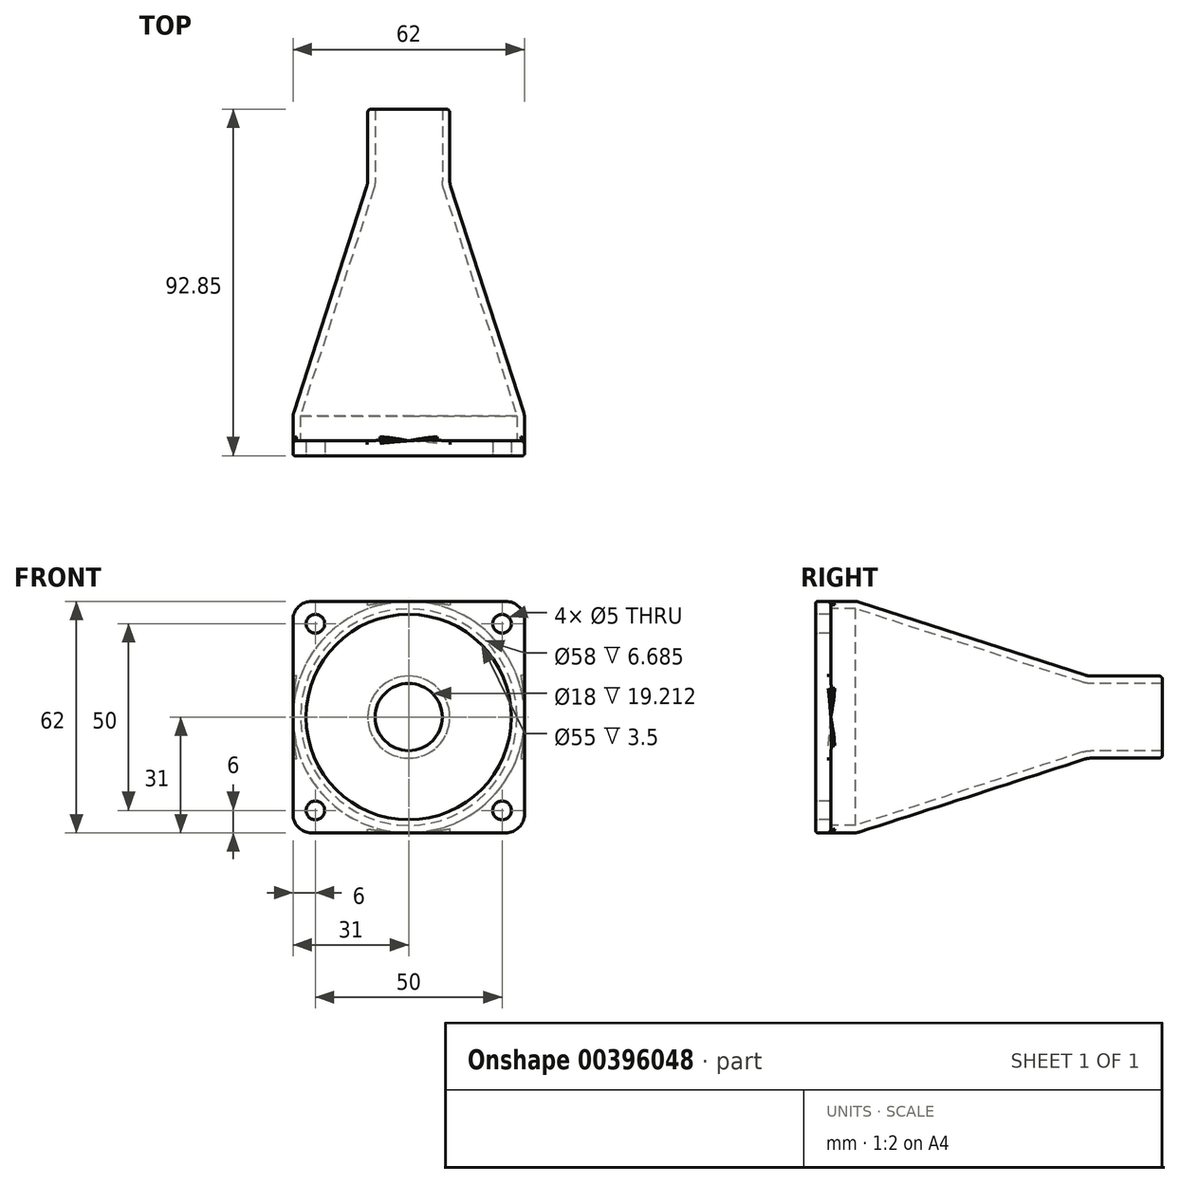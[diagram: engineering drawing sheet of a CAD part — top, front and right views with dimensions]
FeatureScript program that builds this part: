
annotation { "Feature Type Name" : "Feature", "Feature Type Description" : "" }
export const myFeature = defineFeature(function(context is Context, id is Id, definition is map)
    precondition{}
    {
        {
            var Q0;
            Q0=qCreatedBy(makeId("Top.planeOp"),FACE);
            var sketch = newSketch(context, id + "F0", { "sketchPlane" : qUnion([Q0])});
            skLineSegment(sketch, "E0", {"start": v(-31, 0) * mm, "end": v(-31, 7) * mm});
            skLineSegment(sketch, "E1", {"start": v(-31, 7) * mm, "end": v(-11, 68.85) * mm});
            skLineSegment(sketch, "E2", {"start": v(-11, 68.85) * mm, "end": v(-11, 88.85) * mm});
            skLineSegment(sketch, "E3.0", {"start": v(-9, 68.53) * mm, "end": v(-9, 88.85) * mm});
            skLineSegment(sketch, "E3.1", {"start": v(-29, 6.68) * mm, "end": v(-9, 68.53) * mm});
            skLineSegment(sketch, "E3.2", {"start": v(-29, 0) * mm, "end": v(-29, 6.68) * mm});
            skLineSegment(sketch, "E4", {"start": v(-31, 0) * mm, "end": v(-29, 0) * mm});
            skLineSegment(sketch, "E5", {"start": v(-11, 88.85) * mm, "end": v(-9, 88.85) * mm});
            skLineSegment(sketch, "E6", {"start": v(0, 0) * mm, "end": v(0, 51.98) * mm, "construction": true});
            skSolve(sketch);
        }
        {
            var Q0;
            Q0=makeQuery(id+"F0.imprint","IMPRINT",FACE,{"disambiguationData":[TD([[makeQuery(id+"F0.imprint","IMPRINT",EDGE,{"derivedFrom":sQuery(id+"F0.wireOp",EDGE,"E0")}),-1.0]])]});
            var Q1;
            Q1=sQuery(id+"F0.wireOp",EDGE,"E6");
            revolve(context, id + "F1", {"entities" : qUnion([Q0]), "axis" : qUnion([Q1]), "revolveType" : RevolveType.FULL});
        }
        {
            var Q0;
            Q0=makeQuery(id+"F1.opRevolve","SWEPT_EDGE",EDGE,{"disambiguationData":[OSD([sQuery(id+"F0.wireOp",EDGE,"E2"),sQuery(id+"F0.wireOp",EDGE,"E5")])]});
            fillet(context, id + "F2", {"entities" : qUnion([Q0]), "radius" : 1 * mm, "tangentPropagation" : true, "allowEdgeOverflow" : false});
        }
        {
            var Q0;
            Q0=makeQuery(id+"F1.opRevolve","SWEPT_EDGE",EDGE,{"disambiguationData":[OSD([sQuery(id+"F0.wireOp",EDGE,"E3.0"),sQuery(id+"F0.wireOp",EDGE,"E3.1")])]});
            fillet(context, id + "F3", {"entities" : qUnion([Q0]), "radius" : 7 * mm, "tangentPropagation" : true, "allowEdgeOverflow" : false});
        }
        {
            var Q0;
            Q0=qCreatedBy(makeId("Front.planeOp"),FACE);
            var sketch = newSketch(context, id + "F4", { "sketchPlane" : qUnion([Q0])});
            skLineSegment(sketch, "E7.bottom", {"start": v(-31, 31) * mm, "end": v(31, 31) * mm});
            skLineSegment(sketch, "E7.top", {"start": v(-31, -31) * mm, "end": v(31, -31) * mm});
            skLineSegment(sketch, "E7.left", {"start": v(-31, 31) * mm, "end": v(-31, -31) * mm});
            skLineSegment(sketch, "E7.right", {"start": v(31, 31) * mm, "end": v(31, -31) * mm});
            skPoint(sketch, "E7.middle", {"position": v(0, 0) * mm});
            skSolve(sketch);
        }
        {
            var Q0;
            Q0 = qSketchRegion(id + "F4", true);
            extrude(context, id + "F5", {"entities" : qUnion([Q0]), "operationType" : NewBodyOperationType.ADD, "depth" : 4 * mm});
        }
        {
            var Q0;
            Q0=makeQuery(id+"F5.opExtrude","SWEPT_EDGE",EDGE,{"disambiguationData":[OSD([sQuery(id+"F4.wireOp",EDGE,"E7.bottom"),sQuery(id+"F4.wireOp",EDGE,"E7.left")])]});
            var Q1;
            Q1=makeQuery(id+"F5.opExtrude","SWEPT_EDGE",EDGE,{"disambiguationData":[OSD([sQuery(id+"F4.wireOp",EDGE,"E7.top"),sQuery(id+"F4.wireOp",EDGE,"E7.left")])]});
            var Q2;
            Q2=makeQuery(id+"F5.opExtrude","SWEPT_EDGE",EDGE,{"disambiguationData":[OSD([sQuery(id+"F4.wireOp",EDGE,"E7.top"),sQuery(id+"F4.wireOp",EDGE,"E7.right")])]});
            var Q3;
            Q3=makeQuery(id+"F5.opExtrude","SWEPT_EDGE",EDGE,{"disambiguationData":[OSD([sQuery(id+"F4.wireOp",EDGE,"E7.bottom"),sQuery(id+"F4.wireOp",EDGE,"E7.right")])]});
            fillet(context, id + "F6", {"entities" : qUnion([Q0, Q1, Q2, Q3]), "radius" : 5 * mm, "tangentPropagation" : true, "allowEdgeOverflow" : false});
        }
        {
            var Q0;
            {var subQ0=sQuery(id+"F0.wireOp",EDGE,"E0");var subQ1=sQuery(id+"F4.wireOp",EDGE,"E7.left");var subQ2=sQuery(id+"F4.wireOp",EDGE,"E7.top");Q0=makeQuery(id+"F5.boolean.opBoolean","SPLIT",EDGE,{"disambiguationData":[TD([makeQuery(id+"F1.opRevolve","SWEPT_FACE",FACE,{"disambiguationData":[OSD([subQ0])]}),makeQuery(id+"F5.opExtrude","CAP_FACE",FACE,{"disambiguationData":[OSD([sQuery(id+"F4.wireOp",EDGE,"E7.bottom"),subQ2,subQ1,sQuery(id+"F4.wireOp",EDGE,"E7.right")])],"isStart":true}),makeQuery(id+"F5.opExtrude","SWEPT_FACE",FACE,{"disambiguationData":[OSD([subQ2])]}),makeQuery(id+"F5.opExtrude","SWEPT_FACE",FACE,{"disambiguationData":[OSD([subQ1])]})])],"derivedFrom":makeQuery(id+"F1.opRevolve","SWEPT_EDGE",EDGE,{"disambiguationData":[OSD([subQ0,sQuery(id+"F0.wireOp",EDGE,"E4")])]})});}
            fillet(context, id + "F7", {"entities" : qUnion([Q0]), "radius" : 1 * mm, "tangentPropagation" : true, "allowEdgeOverflow" : false});
        }
        {
            var Q0;
            Q0=makeQuery(id+"F5.opExtrude","CAP_FACE",FACE,{"disambiguationData":[OSD([sQuery(id+"F4.wireOp",EDGE,"E7.bottom"),sQuery(id+"F4.wireOp",EDGE,"E7.top"),sQuery(id+"F4.wireOp",EDGE,"E7.left"),sQuery(id+"F4.wireOp",EDGE,"E7.right")])],"isStart":false});
            var sketch = newSketch(context, id + "F8", { "sketchPlane" : qUnion([Q0])});
            skLineSegment(sketch, "E8", {"start": v(0, 0) * mm, "end": v(0, -56.81) * mm, "construction": true});
            skLineSegment(sketch, "E9", {"start": v(0, 0) * mm, "end": v(0, 53.46) * mm, "construction": true});
            skLineSegment(sketch, "E10", {"start": v(0, 0) * mm, "end": v(70, 0) * mm, "construction": true});
            skLineSegment(sketch, "E11", {"start": v(0, 0) * mm, "end": v(-72.23, 0) * mm, "construction": true});
            skLineSegment(sketch, "E12", {"start": v(-72.23, 0) * mm, "end": v(-72.23, -1.04) * mm, "construction": true});
            skLineSegment(sketch, "E13.0", {"start": v(25, 0) * mm, "end": v(25, 53.46) * mm, "construction": true});
            skLineSegment(sketch, "E13.1", {"start": v(25, 0) * mm, "end": v(25, -56.81) * mm, "construction": true});
            skLineSegment(sketch, "E14.0", {"start": v(0, -25) * mm, "end": v(70, -25) * mm, "construction": true});
            skLineSegment(sketch, "E14.1", {"start": v(0, -25) * mm, "end": v(-72.23, -25) * mm, "construction": true});
            skLineSegment(sketch, "E15.0", {"start": v(0, 25) * mm, "end": v(70, 25) * mm, "construction": true});
            skCircle(sketch, "E16", {"center": v(25, -25) * mm, "radius": 2.5 * mm});
            skCircle(sketch, "E17", {"center": v(25, 25) * mm, "radius": 2.5 * mm});
            skLineSegment(sketch, "E18.0", {"start": v(-25, 0) * mm, "end": v(-25, 53.46) * mm, "construction": true});
            skLineSegment(sketch, "E18.1", {"start": v(-25, 0) * mm, "end": v(-25, -56.81) * mm, "construction": true});
            skLineSegment(sketch, "E19.0", {"start": v(0, 25) * mm, "end": v(-72.23, 25) * mm, "construction": true});
            skCircle(sketch, "E20", {"center": v(-25, -25) * mm, "radius": 2.5 * mm});
            skCircle(sketch, "E21", {"center": v(-25, 25) * mm, "radius": 2.5 * mm});
            skSolve(sketch);
        }
        {
            var Q0;
            Q0=makeQuery(id+"F8.imprint","IMPRINT",FACE,{"disambiguationData":[TD([[makeQuery(id+"F8.imprint","IMPRINT",EDGE,{"derivedFrom":sQuery(id+"F8.wireOp",EDGE,"sRCQpmkt-oVAr-W0FF-cRiP-k1k2mR1TycIy")}),1.0]])]});
            var Q1;
            Q1=makeQuery(id+"F8.imprint","IMPRINT",FACE,{"disambiguationData":[TD([[makeQuery(id+"F8.imprint","IMPRINT",EDGE,{"derivedFrom":sQuery(id+"F8.wireOp",EDGE,"WBqi3IDt-zzWq-eJCS-Yybi-qVEHdroCNbEw")}),1.0]])]});
            var Q2;
            Q2=makeQuery(id+"F8.imprint","IMPRINT",FACE,{"disambiguationData":[TD([[makeQuery(id+"F8.imprint","IMPRINT",EDGE,{"derivedFrom":sQuery(id+"F8.wireOp",EDGE,"Cz0v3rXi-JlpB-wq7o-73FV-5aPHxsVT8n9k")}),1.0]])]});
            var Q3;
            Q3=makeQuery(id+"F8.imprint","IMPRINT",FACE,{"disambiguationData":[TD([[makeQuery(id+"F8.imprint","IMPRINT",EDGE,{"derivedFrom":sQuery(id+"F8.wireOp",EDGE,"pcazJkX5-W9sn-ZT1S-FBYo-WmBN8pOrwBYN")}),1.0]])]});
            var Q4;
            Q4=makeQuery(id+"F8.imprint","IMPRINT",FACE,{"disambiguationData":[TD([[makeQuery(id+"F8.imprint","IMPRINT",EDGE,{"derivedFrom":sQuery(id+"F8.wireOp",EDGE,"E17")}),1.0]])]});
            var Q5;
            Q5=makeQuery(id+"F8.imprint","IMPRINT",FACE,{"disambiguationData":[TD([[makeQuery(id+"F8.imprint","IMPRINT",EDGE,{"derivedFrom":sQuery(id+"F8.wireOp",EDGE,"E21")}),1.0]])]});
            var Q6;
            Q6=makeQuery(id+"F8.imprint","IMPRINT",FACE,{"disambiguationData":[TD([[makeQuery(id+"F8.imprint","IMPRINT",EDGE,{"derivedFrom":sQuery(id+"F8.wireOp",EDGE,"E16")}),1.0]])]});
            var Q7;
            Q7=makeQuery(id+"F8.imprint","IMPRINT",FACE,{"disambiguationData":[TD([[makeQuery(id+"F8.imprint","IMPRINT",EDGE,{"derivedFrom":sQuery(id+"F8.wireOp",EDGE,"E20")}),1.0]])]});
            extrude(context, id + "F9", {"entities" : qUnion([Q0, Q1, Q2, Q3, Q4, Q5, Q6, Q7]), "operationType" : NewBodyOperationType.REMOVE, "endBound" : BoundingType.THROUGH_ALL, "oppositeDirection" : true, "depth" : 25 * mm});
        }
        {
            var Q0;
            {var subQ0=sQuery(id+"F4.wireOp",EDGE,"E7.left");var subQ1=sQuery(id+"F4.wireOp",EDGE,"E7.top");Q0=makeQuery(id+"F5.boolean.opBoolean","SPLIT",EDGE,{"disambiguationData":[TD([makeQuery(id+"F5.opExtrude","SWEPT_FACE",FACE,{"disambiguationData":[OSD([subQ1])]})])],"derivedFrom":makeQuery(id+"F5.opExtrude","CAP_EDGE",EDGE,{"disambiguationData":[OSD([subQ0])],"isStart":true})});}
            var Q1;
            {var subQ0=sQuery(id+"F4.wireOp",EDGE,"E7.right");var subQ1=sQuery(id+"F4.wireOp",EDGE,"E7.top");Q1=makeQuery(id+"F5.boolean.opBoolean","SPLIT",EDGE,{"disambiguationData":[TD([makeQuery(id+"F5.opExtrude","SWEPT_FACE",FACE,{"disambiguationData":[OSD([subQ0])]})])],"derivedFrom":makeQuery(id+"F5.opExtrude","CAP_EDGE",EDGE,{"disambiguationData":[OSD([subQ1])],"isStart":true})});}
            var Q2;
            {var subQ0=sQuery(id+"F4.wireOp",EDGE,"E7.left");var subQ1=sQuery(id+"F4.wireOp",EDGE,"E7.bottom");Q2=makeQuery(id+"F5.boolean.opBoolean","SPLIT",EDGE,{"disambiguationData":[TD([makeQuery(id+"F5.opExtrude","SWEPT_FACE",FACE,{"disambiguationData":[OSD([subQ1])]})])],"derivedFrom":makeQuery(id+"F5.opExtrude","CAP_EDGE",EDGE,{"disambiguationData":[OSD([subQ0])],"isStart":true})});}
            var Q3;
            {var subQ0=sQuery(id+"F4.wireOp",EDGE,"E7.bottom");var subQ1=sQuery(id+"F4.wireOp",EDGE,"E7.right");Q3=makeQuery(id+"F5.boolean.opBoolean","SPLIT",EDGE,{"disambiguationData":[TD([makeQuery(id+"F5.opExtrude","SWEPT_FACE",FACE,{"disambiguationData":[OSD([subQ0])]})])],"derivedFrom":makeQuery(id+"F5.opExtrude","CAP_EDGE",EDGE,{"disambiguationData":[OSD([subQ1])],"isStart":true})});}
            fillet(context, id + "F10", {"entities" : qUnion([Q0, Q1, Q2, Q3]), "radius" : 1 * mm, "tangentPropagation" : true, "allowEdgeOverflow" : false});
        }
        {
            var Q0;
            Q0=makeQuery(id+"F5.opExtrude","CAP_FACE",FACE,{"disambiguationData":[OSD([sQuery(id+"F4.wireOp",EDGE,"E7.bottom"),sQuery(id+"F4.wireOp",EDGE,"E7.top"),sQuery(id+"F4.wireOp",EDGE,"E7.left"),sQuery(id+"F4.wireOp",EDGE,"E7.right")])],"isStart":false});
            var sketch = newSketch(context, id + "F11", { "sketchPlane" : qUnion([Q0])});
            skCircle(sketch, "E22", {"center": v(0, 0) * mm, "radius": 27.5 * mm});
            skSolve(sketch);
        }
        {
            var Q0;
            Q0=makeQuery(id+"F11.imprint","IMPRINT",FACE,{"disambiguationData":[TD([[makeQuery(id+"F11.imprint","IMPRINT",EDGE,{"derivedFrom":sQuery(id+"F11.wireOp",EDGE,"E22")}),1.0]])]});
            extrude(context, id + "F12", {"entities" : qUnion([Q0]), "operationType" : NewBodyOperationType.REMOVE, "endBound" : BoundingType.UP_TO_NEXT, "oppositeDirection" : true, "depth" : 25 * mm});
        }
        {
            var Q0;
            Q0=makeQuery(id+"F5.opExtrude","CAP_FACE",FACE,{"disambiguationData":[OSD([sQuery(id+"F4.wireOp",EDGE,"E7.bottom"),sQuery(id+"F4.wireOp",EDGE,"E7.top"),sQuery(id+"F4.wireOp",EDGE,"E7.left"),sQuery(id+"F4.wireOp",EDGE,"E7.right")])],"isStart":false});
            fillet(context, id + "F13", {"entities" : qUnion([Q0]), "radius" : .5 * mm, "tangentPropagation" : true, "allowEdgeOverflow" : false});
        }
        {
            var Q0;
            Q0=makeQuery(id+"F1.opRevolve","SWEPT_EDGE",EDGE,{"disambiguationData":[OSD([sQuery(id+"F0.wireOp",EDGE,"E0"),sQuery(id+"F0.wireOp",EDGE,"E1")])]});
            fillet(context, id + "F14", {"entities" : qUnion([Q0]), "radius" : 5 * mm, "tangentPropagation" : true, "allowEdgeOverflow" : false});
        }
        {
            var Q0;
            Q0=makeQuery(id+"F1.opRevolve","SWEPT_EDGE",EDGE,{"disambiguationData":[OSD([sQuery(id+"F0.wireOp",EDGE,"E1"),sQuery(id+"F0.wireOp",EDGE,"E2")])]});
            fillet(context, id + "F15", {"entities" : qUnion([Q0]), "radius" : 5 * mm, "tangentPropagation" : true, "allowEdgeOverflow" : false});
        }
        {
            var Q0;
            {var subQ0=sQuery(id+"F4.wireOp",EDGE,"E7.bottom");var subQ1=sQuery(id+"F4.wireOp",EDGE,"E7.right");var subQ2=makeQuery(id+"F5.opExtrude","CAP_FACE",FACE,{"disambiguationData":[OSD([subQ0,sQuery(id+"F4.wireOp",EDGE,"E7.top"),sQuery(id+"F4.wireOp",EDGE,"E7.left"),subQ1])],"isStart":true});Q0=makeQuery(id+"F9.boolean.opBoolean","INTERSECT",EDGE,{"derivedFrom":[makeQuery(id+"F5.boolean.opBoolean","SPLIT",FACE,{"disambiguationData":[TD([makeQuery(id+"F1.opRevolve","SWEPT_FACE",FACE,{"disambiguationData":[OSD([sQuery(id+"F0.wireOp",EDGE,"E0")])]}),makeQuery(id+"F5.opExtrude","SWEPT_FACE",FACE,{"disambiguationData":[OSD([subQ0])]}),subQ2,makeQuery(id+"F5.opExtrude","SWEPT_FACE",FACE,{"disambiguationData":[OSD([subQ1])]})])],"derivedFrom":subQ2}),makeQuery(id+"F9.opExtrude","SWEPT_FACE",FACE,{"disambiguationData":[OSD([sQuery(id+"F8.wireOp",EDGE,"E17")])]})]});}
            var Q1;
            {var subQ0=sQuery(id+"F4.wireOp",EDGE,"E7.bottom");var subQ1=sQuery(id+"F4.wireOp",EDGE,"E7.left");var subQ2=makeQuery(id+"F5.opExtrude","CAP_FACE",FACE,{"disambiguationData":[OSD([subQ0,sQuery(id+"F4.wireOp",EDGE,"E7.top"),subQ1,sQuery(id+"F4.wireOp",EDGE,"E7.right")])],"isStart":true});Q1=makeQuery(id+"F9.boolean.opBoolean","INTERSECT",EDGE,{"derivedFrom":[makeQuery(id+"F5.boolean.opBoolean","SPLIT",FACE,{"disambiguationData":[TD([makeQuery(id+"F1.opRevolve","SWEPT_FACE",FACE,{"disambiguationData":[OSD([sQuery(id+"F0.wireOp",EDGE,"E0")])]}),makeQuery(id+"F5.opExtrude","SWEPT_FACE",FACE,{"disambiguationData":[OSD([subQ0])]}),subQ2,makeQuery(id+"F5.opExtrude","SWEPT_FACE",FACE,{"disambiguationData":[OSD([subQ1])]})])],"derivedFrom":subQ2}),makeQuery(id+"F9.opExtrude","SWEPT_FACE",FACE,{"disambiguationData":[OSD([sQuery(id+"F8.wireOp",EDGE,"E21")])]})]});}
            var Q2;
            {var subQ0=sQuery(id+"F4.wireOp",EDGE,"E7.left");var subQ1=sQuery(id+"F4.wireOp",EDGE,"E7.top");var subQ2=makeQuery(id+"F5.opExtrude","CAP_FACE",FACE,{"disambiguationData":[OSD([sQuery(id+"F4.wireOp",EDGE,"E7.bottom"),subQ1,subQ0,sQuery(id+"F4.wireOp",EDGE,"E7.right")])],"isStart":true});Q2=makeQuery(id+"F9.boolean.opBoolean","INTERSECT",EDGE,{"derivedFrom":[makeQuery(id+"F5.boolean.opBoolean","SPLIT",FACE,{"disambiguationData":[TD([makeQuery(id+"F1.opRevolve","SWEPT_FACE",FACE,{"disambiguationData":[OSD([sQuery(id+"F0.wireOp",EDGE,"E0")])]}),subQ2,makeQuery(id+"F5.opExtrude","SWEPT_FACE",FACE,{"disambiguationData":[OSD([subQ1])]}),makeQuery(id+"F5.opExtrude","SWEPT_FACE",FACE,{"disambiguationData":[OSD([subQ0])]})])],"derivedFrom":subQ2}),makeQuery(id+"F9.opExtrude","SWEPT_FACE",FACE,{"disambiguationData":[OSD([sQuery(id+"F8.wireOp",EDGE,"E20")])]})]});}
            var Q3;
            {var subQ0=sQuery(id+"F4.wireOp",EDGE,"E7.right");var subQ1=sQuery(id+"F4.wireOp",EDGE,"E7.top");var subQ2=makeQuery(id+"F5.opExtrude","CAP_FACE",FACE,{"disambiguationData":[OSD([sQuery(id+"F4.wireOp",EDGE,"E7.bottom"),subQ1,sQuery(id+"F4.wireOp",EDGE,"E7.left"),subQ0])],"isStart":true});Q3=makeQuery(id+"F9.boolean.opBoolean","INTERSECT",EDGE,{"derivedFrom":[makeQuery(id+"F5.boolean.opBoolean","SPLIT",FACE,{"disambiguationData":[TD([makeQuery(id+"F1.opRevolve","SWEPT_FACE",FACE,{"disambiguationData":[OSD([sQuery(id+"F0.wireOp",EDGE,"E0")])]}),subQ2,makeQuery(id+"F5.opExtrude","SWEPT_FACE",FACE,{"disambiguationData":[OSD([subQ1])]}),makeQuery(id+"F5.opExtrude","SWEPT_FACE",FACE,{"disambiguationData":[OSD([subQ0])]})])],"derivedFrom":subQ2}),makeQuery(id+"F9.opExtrude","SWEPT_FACE",FACE,{"disambiguationData":[OSD([sQuery(id+"F8.wireOp",EDGE,"E16")])]})]});}
            fillet(context, id + "F16", {"entities" : qUnion([Q0, Q1, Q2, Q3]), "radius" : .2 * mm, "tangentPropagation" : true, "allowEdgeOverflow" : false});
        }
    });
